SOLIDWORKS PART (.sldprt)
format: sldprt  version: not decoded by parser v0  size: 227,840 bytes
history: native  units: mm
features: sketch x5, extrude x4, fillet x2, material x1 (+11 scaffold rows collapsed)
feature tree (23):
  scaffold x11  (default folders/planes/origin — collapsed)
  material  "Material <not specified>"
  sketch  "Sketch1"  dims[D1=10.0mm]
  extrude  "Boss-Extrude1"  Depth=2mm
  sketch  "Sketch2"  dims[D1=10.0mm]
  extrude  "Boss-Extrude2"  [1 undecoded]
  fillet  "Fillet1"  Radius=2mm
  sketch  "Sketch3"  dims[D2=7.0mm D1=7.0mm]
  extrude  "Boss-Extrude3"  Depth=2mm
  sketch  "Sketch5"  dims[c1.D1=2.0mm c2.D1=2.25mm c2.D5=3.0mm c2.D6=2.54mm c2.D7=5.0mm]
  sketch  "Sketch8"  dims[D1=8.0mm]
  extrude  "Boss-Extrude4"  [1 undecoded]
  fillet  "Fillet2"  Radius=8mm
decode coverage: 9 of 11 modeling features carry decoded parameters
note: 2 parameter values undecoded
note: suppression state not decoded; provenance and decode notes live in map.json
